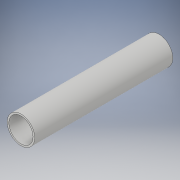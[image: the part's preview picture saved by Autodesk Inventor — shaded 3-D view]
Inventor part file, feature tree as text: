
AUTODESK INVENTOR PART (.ipt)
format: ipt  version: 2019 (Build 230136000, 136)  size: 97,280 bytes
history: native  units: mm
features: extrude x1, sketch x1
ambient origin geometry x8: Origin, YZ Plane, XZ Plane, XY Plane, X Axis, Y Axis, Z Axis, Center Point
bodies: Solide1 (feature_tree)
feature tree (2):
  extrude  "Extrusion1"  Depth=2.5mm
  sketch  "Esquisse1"
